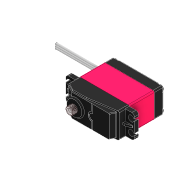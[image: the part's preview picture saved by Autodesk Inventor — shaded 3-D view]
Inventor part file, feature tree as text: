
AUTODESK INVENTOR PART (.ipt)
format: ipt  version: 2021 (Build 250183000, 183)  size: 1,463,808 bytes
history: native  units: mm
features: other x40, mirror x3, fillet x2
ambient origin geometry x8: Origin, YZ Plane, XZ Plane, XY Plane, X Axis, Y Axis, Z Axis, Center Point
bodies: Body1 (feature_tree), Body2 (feature_tree), Body3 (feature_tree), Body4 (feature_tree), Body5 (feature_tree), Body6 (feature_tree), Body7 (feature_tree), Body8 (feature_tree), Body9 (feature_tree), Body10 (feature_tree), Body11 (feature_tree), Body12 (feature_tree)
feature tree (45):
  other  "Твердое тело1"
  mirror  "Mirror4[2]"
  other  "Непосредственное редактирование1"
  other  "Непосредственное редактирование5"
  other  "Непосредственное редактирование6"
  other  "Непосредственное редактирование8"
  other  "Непосредственное редактирование9"
  other  "Непосредственное редактирование10"
  other  "Непосредственное редактирование11"
  other  "Непосредственное редактирование12"
  other  "Твердое тело2"
  other  "Твердое тело3"
  other  "Твердое тело4"
  other  "Твердое тело5"
  other  "Твердое тело6"
  other  "Твердое тело7"
  other  "Твердое тело8"
  other  "Твердое тело9"
  other  "Твердое тело10"
  other  "Твердое тело11"
  other  "Твердое тело12"
  other  "Spline M3 Tapped Hole"
  other  "Metal Servo Body"
  fillet  "Fillet5"  Radius=0.1mm
  mirror  "Mirror3"
  mirror  "Mirror4[1]"
  other  "Label"
  fillet  "Fillet6"  [1 undecoded]
  other  "Cut-Extrude10"
  other  "Wire[1]"
  other  "Wire[2]"
  other  "Wire[3]"
  other  "Размер1"
  other  "Перенос7"
  other  "Перенос8"
  other  "Размер2"
  other  "Размер5"
  other  "Размер6"
  other  "Размер7"
  other  "Размер8"
  other  "Размер9"
  other  "Размер10"
  other  "Размер11"
  other  "Размер12"
  other  "Размер13"
note: 1 required parameter value undecoded (feature->parameter linkage not recoverable at this tier; creation-order binding heuristic only, values carry confidence <= 0.55)
